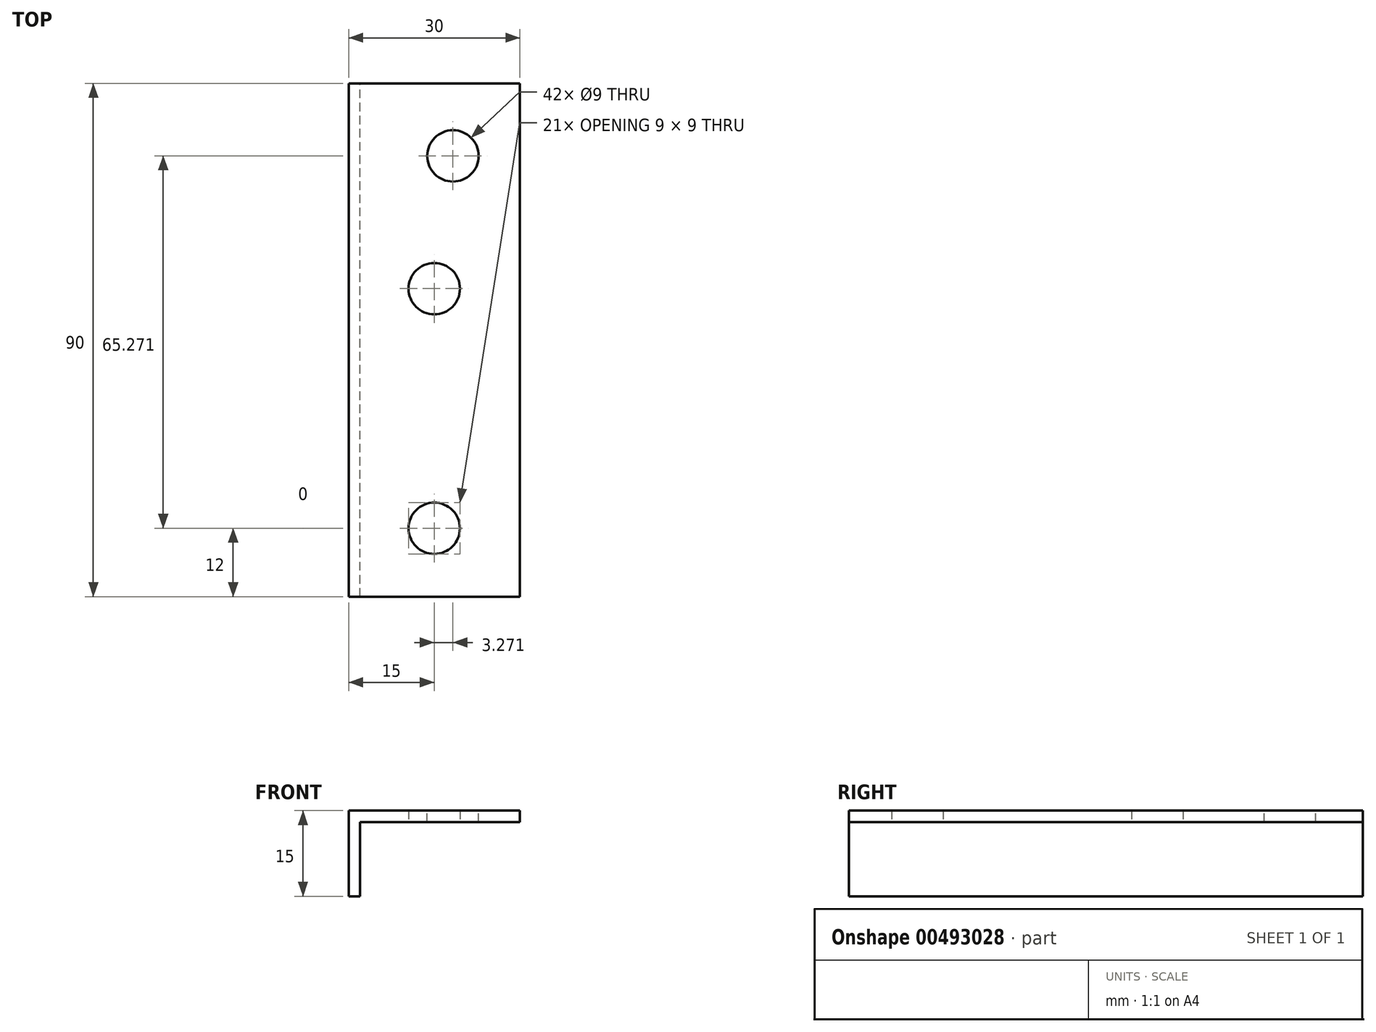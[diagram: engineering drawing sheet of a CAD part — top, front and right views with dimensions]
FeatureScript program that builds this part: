
annotation { "Feature Type Name" : "Feature", "Feature Type Description" : "" }
export const myFeature = defineFeature(function(context is Context, id is Id, definition is map)
    precondition{}
    {
        {
            var Q0;
            Q0=qCreatedBy(makeId("Front.planeOp"),FACE);
            var sketch = newSketch(context, id + "F0", { "sketchPlane" : qUnion([Q0])});
            skLineSegment(sketch, "E0", {"start": v(0, -15) * mm, "end": v(0, 0) * mm});
            skLineSegment(sketch, "E1", {"start": v(0, 0) * mm, "end": v(30, 0) * mm});
            skLineSegment(sketch, "E2", {"start": v(30, 0) * mm, "end": v(30, -2) * mm});
            skLineSegment(sketch, "E3", {"start": v(30, -2) * mm, "end": v(2, -2) * mm});
            skLineSegment(sketch, "E4", {"start": v(2, -2) * mm, "end": v(2, -15) * mm});
            skLineSegment(sketch, "E5", {"start": v(2, -15) * mm, "end": v(0, -15) * mm});
            skSolve(sketch);
        }
        {
            var Q0;
            Q0 = qSketchRegion(id + "F0", true);
            extrude(context, id + "F1", {"entities" : qUnion([Q0]), "depth" : 90 * mm});
        }
        {
            var Q0;
            Q0=makeQuery(id+"F1.opExtrude","SWEPT_FACE",FACE,{"disambiguationData":[OSD([sQuery(id+"F0.wireOp",EDGE,"E3")])]});
            var sketch = newSketch(context, id + "F2", { "sketchPlane" : qUnion([Q0])});
            skLineSegment(sketch, "E6", {"start": v(15, 90) * mm, "end": v(15, 0) * mm, "construction": true});
            skCircle(sketch, "E7", {"center": v(15, 78) * mm, "radius": 4.5 * mm});
            skCircle(sketch, "E8", {"center": v(15, 36) * mm, "radius": 4.5 * mm});
            skSolve(sketch);
        }
        {
            var Q0;
            Q0 = qSketchRegion(id + "F2", true);
            extrude(context, id + "F3", {"entities" : qUnion([Q0]), "operationType" : NewBodyOperationType.REMOVE, "endBound" : BoundingType.THROUGH_ALL, "oppositeDirection" : true, "depth" : 25 * mm});
        }
        {
            var Q0;
            Q0=makeQuery(id+"F1.opExtrude","SWEPT_FACE",FACE,{"disambiguationData":[OSD([sQuery(id+"F0.wireOp",EDGE,"E1")])]});
            var sketch = newSketch(context, id + "F4", { "sketchPlane" : qUnion([Q0])});
            skLineSegment(sketch, "E9", {"start": v(15, -36) * mm, "end": v(18.27, -12.73) * mm, "construction": true});
            skLineSegment(sketch, "E10", {"start": v(15, 0) * mm, "end": v(15, -36) * mm, "construction": true});
            skCircle(sketch, "E11", {"center": v(18.27, -12.73) * mm, "radius": 4.5 * mm});
            skSolve(sketch);
        }
        {
            var Q0;
            Q0 = qSketchRegion(id + "F4", true);
            extrude(context, id + "F5", {"entities" : qUnion([Q0]), "operationType" : NewBodyOperationType.REMOVE, "endBound" : BoundingType.THROUGH_ALL, "oppositeDirection" : true, "depth" : 25 * mm});
        }
    });
